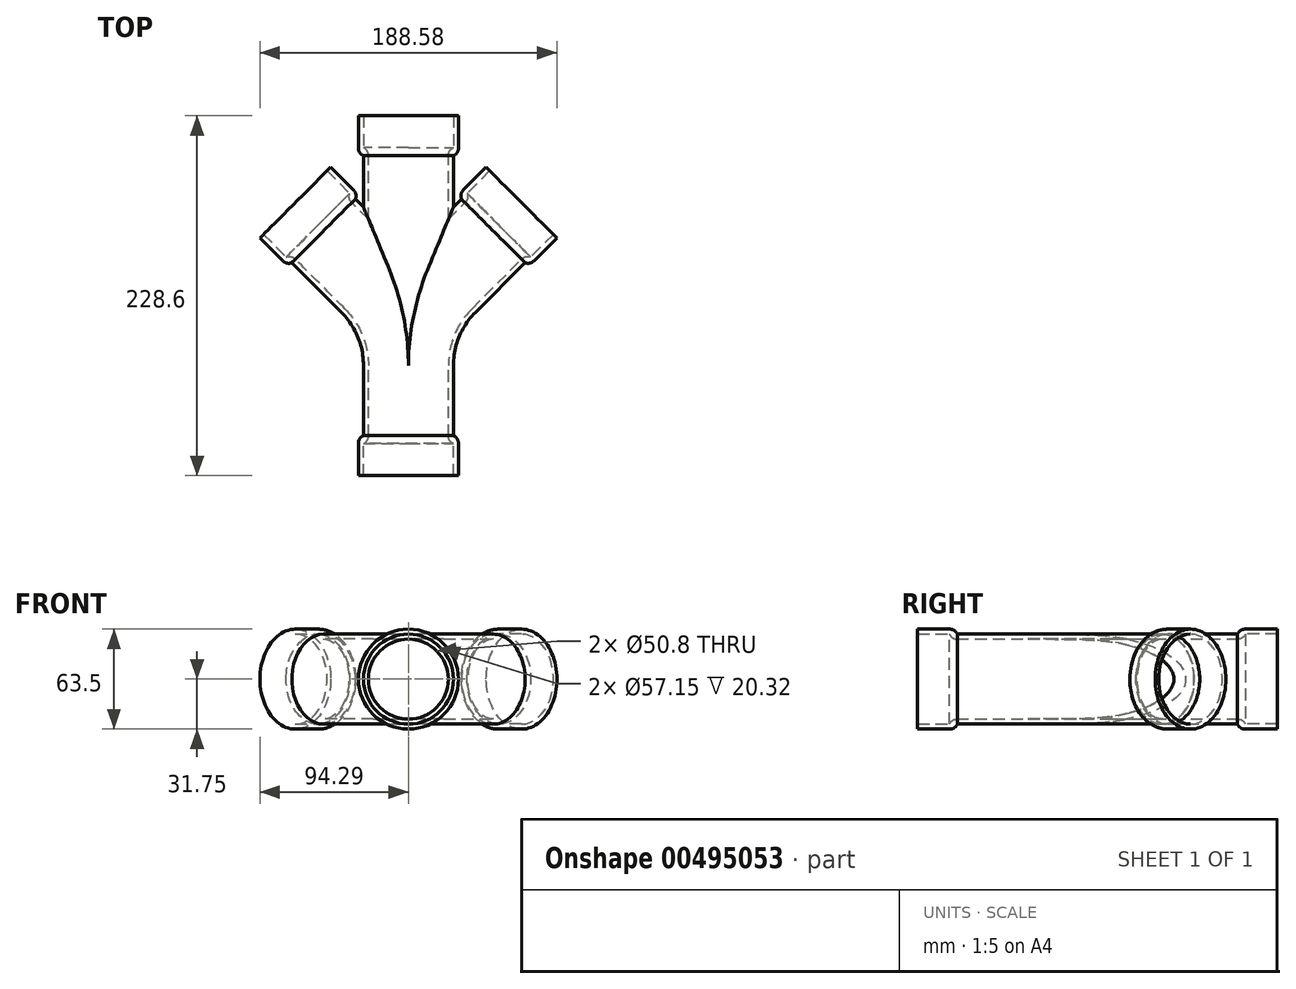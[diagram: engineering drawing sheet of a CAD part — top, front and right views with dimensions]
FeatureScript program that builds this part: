
annotation { "Feature Type Name" : "Feature", "Feature Type Description" : "" }
export const myFeature = defineFeature(function(context is Context, id is Id, definition is map)
    precondition{}
    {
        {
            var Q0;
            Q0=qCreatedBy(makeId("Front.planeOp"),FACE);
            var sketch = newSketch(context, id + "F0", { "sketchPlane" : qUnion([Q0])});
            skCircle(sketch, "E0", {"center": v(0, 0) * mm, "radius": 25.4 * mm});
            skCircle(sketch, "E1", {"center": v(0, 0) * mm, "radius": 28.58 * mm});
            skCircle(sketch, "E2", {"center": v(0, 0) * mm, "radius": 31.75 * mm});
            skCircle(sketch, "E3", {"center": v(0, 0) * mm, "radius": 12.7 * mm});
            skSolve(sketch);
        }
        {
            var Q0;
            Q0=qCreatedBy(makeId("Top.planeOp"),FACE);
            var sketch = newSketch(context, id + "F1", { "sketchPlane" : qUnion([Q0])});
            skLineSegment(sketch, "E4", {"start": v(0, 0) * mm, "end": v(0, 177.8) * mm});
            skLineSegment(sketch, "E5", {"start": v(0, 0) * mm, "end": v(0, 44.64) * mm});
            skLineSegment(sketch, "E6.bottom", {"start": v(0, 76.2) * mm, "end": v(53.88, 76.2) * mm});
            skLineSegment(sketch, "E6.top", {"start": v(0, 130.08) * mm, "end": v(53.88, 130.08) * mm});
            skLineSegment(sketch, "E6.left", {"start": v(0, 76.2) * mm, "end": v(0, 130.08) * mm});
            skLineSegment(sketch, "E6.right", {"start": v(53.88, 76.2) * mm, "end": v(53.88, 130.08) * mm});
            skLineSegment(sketch, "E7.bottom", {"start": v(0, 76.2) * mm, "end": v(-53.88, 76.2) * mm});
            skLineSegment(sketch, "E7.top", {"start": v(0, 130.08) * mm, "end": v(-53.88, 130.08) * mm});
            skLineSegment(sketch, "E7.right", {"start": v(-53.88, 76.2) * mm, "end": v(-53.88, 130.08) * mm});
            skLineSegment(sketch, "E8", {"start": v(22.32, 98.52) * mm, "end": v(53.88, 130.08) * mm});
            skLineSegment(sketch, "E9", {"start": v(-22.32, 98.52) * mm, "end": v(-53.88, 130.08) * mm});
            skPoint(sketch, "E10.visualSharp", {"position": v(0, 76.2) * mm});
            skArc(sketch, "E10.filletArc", {"start": v(22.32, 98.52) * mm, "mid": v(5.8, 73.8) * mm, "end": v(0, 44.64) * mm});
            skArc(sketch, "E11.filletArc", {"start": v(0, 44.64) * mm, "mid": v(-5.8, 73.8) * mm, "end": v(-22.32, 98.52) * mm});
            skSolve(sketch);
        }
        {
            var Q0;
            Q0=makeQuery(id+"F0.imprint","IMPRINT",FACE,{"disambiguationData":[TD([[makeQuery(id+"F0.imprint","IMPRINT",EDGE,{"derivedFrom":sQuery(id+"F0.wireOp",EDGE,"E0")}),-1.0]])]});
            var Q1;
            Q1=sQuery(id+"F1.wireOp",EDGE,"E5");
            var Q2;
            Q2=sQuery(id+"F1.wireOp",EDGE,"E10.filletArc");
            var Q3;
            Q3=sQuery(id+"F1.wireOp",EDGE,"E8");
            sweep(context, id + "F2", {"profiles" : qUnion([Q0]), "path" : qUnion([Q1, Q2, Q3])});
        }
        {
            var Q0;
            Q0=makeQuery(id+"F0.imprint","IMPRINT",FACE,{"disambiguationData":[TD([[makeQuery(id+"F0.imprint","IMPRINT",EDGE,{"derivedFrom":sQuery(id+"F0.wireOp",EDGE,"E0")}),-1.0]])]});
            var Q1;
            Q1=sQuery(id+"F1.wireOp",EDGE,"E5");
            var Q2;
            Q2=sQuery(id+"F1.wireOp",EDGE,"E11.filletArc");
            var Q3;
            Q3=sQuery(id+"F1.wireOp",EDGE,"E9");
            sweep(context, id + "F3", {"operationType" : NewBodyOperationType.ADD, "profiles" : qUnion([Q0]), "path" : qUnion([Q1, Q2, Q3])});
        }
        {
            var Q0;
            Q0=makeQuery(id+"F0.imprint","IMPRINT",FACE,{"disambiguationData":[TD([[makeQuery(id+"F0.imprint","IMPRINT",EDGE,{"derivedFrom":sQuery(id+"F0.wireOp",EDGE,"E0")}),-1.0]])]});
            var Q1;
            Q1=sQuery(id+"F1.wireOp",EDGE,"E4");
            sweep(context, id + "F4", {"operationType" : NewBodyOperationType.ADD, "profiles" : qUnion([Q0]), "path" : qUnion([Q1])});
        }
        {
            var Q0;
            Q0=makeQuery(id+"F0.imprint","IMPRINT",FACE,{"disambiguationData":[TD([[makeQuery(id+"F0.imprint","IMPRINT",EDGE,{"derivedFrom":sQuery(id+"F0.wireOp",EDGE,"E0")}),1.0]])]});
            var Q1;
            Q1=makeQuery(id+"F0.imprint","IMPRINT",FACE,{"disambiguationData":[TD([[makeQuery(id+"F0.imprint","IMPRINT",EDGE,{"derivedFrom":sQuery(id+"F0.wireOp",EDGE,"E3")}),1.0]])]});
            var Q2;
            Q2=sQuery(id+"F1.wireOp",EDGE,"E10.filletArc");
            var Q3;
            Q3=sQuery(id+"F1.wireOp",EDGE,"E8");
            var Q4;
            Q4=sQuery(id+"F1.wireOp",EDGE,"E5");
            sweep(context, id + "F5", {"operationType" : NewBodyOperationType.REMOVE, "profiles" : qUnion([Q0, Q1]), "path" : qUnion([Q2, Q3, Q4])});
        }
        {
            var Q0;
            Q0=makeQuery(id+"F0.imprint","IMPRINT",FACE,{"disambiguationData":[TD([[makeQuery(id+"F0.imprint","IMPRINT",EDGE,{"derivedFrom":sQuery(id+"F0.wireOp",EDGE,"E0")}),1.0]])]});
            var Q1;
            Q1=makeQuery(id+"F0.imprint","IMPRINT",FACE,{"disambiguationData":[TD([[makeQuery(id+"F0.imprint","IMPRINT",EDGE,{"derivedFrom":sQuery(id+"F0.wireOp",EDGE,"E3")}),1.0]])]});
            var Q2;
            Q2=sQuery(id+"F1.wireOp",EDGE,"E5");
            var Q3;
            Q3=sQuery(id+"F1.wireOp",EDGE,"E11.filletArc");
            var Q4;
            Q4=sQuery(id+"F1.wireOp",EDGE,"E9");
            sweep(context, id + "F6", {"operationType" : NewBodyOperationType.REMOVE, "profiles" : qUnion([Q0, Q1]), "path" : qUnion([Q2, Q3, Q4])});
        }
        {
            var Q0;
            Q0=makeQuery(id+"F0.imprint","IMPRINT",FACE,{"disambiguationData":[TD([[makeQuery(id+"F0.imprint","IMPRINT",EDGE,{"derivedFrom":sQuery(id+"F0.wireOp",EDGE,"E0")}),1.0]])]});
            var Q1;
            Q1=makeQuery(id+"F0.imprint","IMPRINT",FACE,{"disambiguationData":[TD([[makeQuery(id+"F0.imprint","IMPRINT",EDGE,{"derivedFrom":sQuery(id+"F0.wireOp",EDGE,"E3")}),1.0]])]});
            var Q2;
            Q2=sQuery(id+"F1.wireOp",EDGE,"E4");
            sweep(context, id + "F7", {"operationType" : NewBodyOperationType.REMOVE, "profiles" : qUnion([Q0, Q1]), "path" : qUnion([Q2])});
        }
        {
            var Q0;
            Q0=makeQuery(id+"F0.imprint","IMPRINT",FACE,{"disambiguationData":[TD([[makeQuery(id+"F0.imprint","IMPRINT",EDGE,{"derivedFrom":sQuery(id+"F0.wireOp",EDGE,"E0")}),-1.0]])]});
            extrude(context, id + "F8", {"entities" : qUnion([Q0]), "operationType" : NewBodyOperationType.ADD, "depth" : 5.08 * mm, "offsetDistance" : 25.4 * mm});
        }
        {
            var Q0;
            Q0=makeQuery(id+"F0.imprint","IMPRINT",FACE,{"disambiguationData":[TD([[makeQuery(id+"F0.imprint","IMPRINT",EDGE,{"derivedFrom":sQuery(id+"F0.wireOp",EDGE,"E1")}),-1.0]])]});
            extrude(context, id + "F9", {"entities" : qUnion([Q0]), "operationType" : NewBodyOperationType.ADD, "depth" : 25.4 * mm, "offsetDistance" : 25.4 * mm});
        }
        {
            var Q0;
            Q0=makeQuery(id+"F2.opSweep","CAP_FACE",FACE,{"disambiguationData":[OSD([sQuery(id+"F0.wireOp",EDGE,"E0"),sQuery(id+"F0.wireOp",EDGE,"E1"),sQuery(id+"F1.wireOp",VERTEX,"E8.end")])],"isStart":false});
            var sketch = newSketch(context, id + "F10", { "sketchPlane" : qUnion([Q0])});
            skCircle(sketch, "E12.0", {"center": v(53.88, 0) * mm, "radius": 28.58 * mm});
            skCircle(sketch, "E13.0", {"center": v(53.88, 0) * mm, "radius": 25.4 * mm});
            skCircle(sketch, "E14", {"center": v(53.88, 0) * mm, "radius": 31.75 * mm});
            skSolve(sketch);
        }
        {
            var Q0;
            Q0=makeQuery(id+"F10.imprint","IMPRINT",FACE,{"disambiguationData":[TD([[makeQuery(id+"F10.imprint","IMPRINT",EDGE,{"derivedFrom":sQuery(id+"F10.wireOp",EDGE,"E12.0")}),1.0]])]});
            extrude(context, id + "F11", {"entities" : qUnion([Q0]), "operationType" : NewBodyOperationType.ADD, "depth" : 5.08 * mm, "offsetDistance" : 25.4 * mm});
        }
        {
            var Q0;
            Q0=makeQuery(id+"F10.imprint","IMPRINT",FACE,{"disambiguationData":[TD([[makeQuery(id+"F10.imprint","IMPRINT",EDGE,{"derivedFrom":sQuery(id+"F10.wireOp",EDGE,"E12.0")}),-1.0]])]});
            extrude(context, id + "F12", {"entities" : qUnion([Q0]), "operationType" : NewBodyOperationType.ADD, "depth" : 25.4 * mm, "offsetDistance" : 25.4 * mm});
        }
        {
            var Q0;
            Q0=makeQuery(id+"F4.opSweep","CAP_FACE",FACE,{"disambiguationData":[OSD([sQuery(id+"F0.wireOp",EDGE,"E0"),sQuery(id+"F0.wireOp",EDGE,"E1"),sQuery(id+"F1.wireOp",VERTEX,"E4.end")])],"isStart":false});
            var sketch = newSketch(context, id + "F13", { "sketchPlane" : qUnion([Q0])});
            skCircle(sketch, "E15.0", {"center": v(0, 0) * mm, "radius": 25.4 * mm});
            skCircle(sketch, "E16.0", {"center": v(0, 0) * mm, "radius": 28.58 * mm});
            skCircle(sketch, "E17", {"center": v(0, 0) * mm, "radius": 31.75 * mm});
            skSolve(sketch);
        }
        {
            var Q0;
            Q0=makeQuery(id+"F13.imprint","IMPRINT",FACE,{"disambiguationData":[TD([[makeQuery(id+"F13.imprint","IMPRINT",EDGE,{"derivedFrom":sQuery(id+"F13.wireOp",EDGE,"E15.0")}),1.0]])]});
            extrude(context, id + "F14", {"entities" : qUnion([Q0]), "operationType" : NewBodyOperationType.ADD, "depth" : 5.08 * mm, "offsetDistance" : 25.4 * mm});
        }
        {
            var Q0;
            Q0=makeQuery(id+"F13.imprint","IMPRINT",FACE,{"disambiguationData":[TD([[makeQuery(id+"F13.imprint","IMPRINT",EDGE,{"derivedFrom":sQuery(id+"F13.wireOp",EDGE,"E16.0")}),-1.0]])]});
            extrude(context, id + "F15", {"entities" : qUnion([Q0]), "operationType" : NewBodyOperationType.ADD, "depth" : 25.4 * mm, "offsetDistance" : 25.4 * mm});
        }
        {
            var Q0;
            Q0=makeQuery(id+"F3.opSweep","CAP_FACE",FACE,{"disambiguationData":[OSD([sQuery(id+"F0.wireOp",EDGE,"E0"),sQuery(id+"F0.wireOp",EDGE,"E1"),sQuery(id+"F1.wireOp",VERTEX,"E9.end")])],"isStart":false});
            var sketch = newSketch(context, id + "F16", { "sketchPlane" : qUnion([Q0])});
            skCircle(sketch, "E18", {"center": v(-53.88, 0) * mm, "radius": 31.75 * mm});
            skSolve(sketch);
        }
        {
            var Q0;
            {var subQ0=sQuery(id+"F1.wireOp",VERTEX,"E9.end");Q0=makeQuery(id+"F16.imprint","IMPRINT",FACE,{"disambiguationData":[TD([[makeQuery(id+"F16.imprint","IMPRINT",EDGE,{"derivedFrom":makeQuery(id+"F3.opSweep","CAP_EDGE",EDGE,{"disambiguationData":[OSD([sQuery(id+"F0.wireOp",EDGE,"E0"),subQ0])],"isStart":false})}),1.0]])]});}
            extrude(context, id + "F17", {"entities" : qUnion([Q0]), "operationType" : NewBodyOperationType.ADD, "depth" : 5.08 * mm, "offsetDistance" : 25.4 * mm});
        }
        {
            var Q0;
            Q0=makeQuery(id+"F16.imprint","IMPRINT",FACE,{"disambiguationData":[TD([[makeQuery(id+"F16.imprint","IMPRINT",EDGE,{"derivedFrom":sQuery(id+"F16.wireOp",EDGE,"E18")}),1.0]])]});
            extrude(context, id + "F18", {"entities" : qUnion([Q0]), "operationType" : NewBodyOperationType.ADD, "depth" : 25.4 * mm, "offsetDistance" : 25.4 * mm});
        }
        {
            var Q0;
            Q0=makeQuery(id+"F15.opExtrude","CAP_EDGE",EDGE,{"disambiguationData":[OSD([sQuery(id+"F13.wireOp",EDGE,"E17")])],"isStart":true});
            var Q1;
            Q1=makeQuery(id+"F18.opExtrude","CAP_EDGE",EDGE,{"disambiguationData":[OSD([sQuery(id+"F16.wireOp",EDGE,"E18")])],"isStart":true});
            var Q2;
            Q2=makeQuery(id+"F12.opExtrude","CAP_EDGE",EDGE,{"disambiguationData":[OSD([sQuery(id+"F10.wireOp",EDGE,"E14")])],"isStart":true});
            var Q3;
            Q3=makeQuery(id+"F9.opExtrude","CAP_EDGE",EDGE,{"disambiguationData":[OSD([sQuery(id+"F0.wireOp",EDGE,"E2")])],"isStart":true});
            var Q4;
            Q4=makeQuery(id+"F14.opExtrude","CAP_EDGE",EDGE,{"disambiguationData":[OSD([sQuery(id+"F13.wireOp",EDGE,"E15.0")])],"isStart":false});
            var Q5;
            Q5=makeQuery(id+"F11.opExtrude","CAP_EDGE",EDGE,{"disambiguationData":[OSD([sQuery(id+"F10.wireOp",EDGE,"E13.0")])],"isStart":false});
            var Q6;
            Q6=makeQuery(id+"F17.opExtrude","CAP_EDGE",EDGE,{"disambiguationData":[OSD([sQuery(id+"F0.wireOp",EDGE,"E0"),sQuery(id+"F1.wireOp",VERTEX,"E9.end")])],"isStart":false});
            var Q7;
            Q7=makeQuery(id+"F8.opExtrude","CAP_EDGE",EDGE,{"disambiguationData":[OSD([sQuery(id+"F0.wireOp",EDGE,"E0")])],"isStart":false});
            fillet(context, id + "F19", {"entities" : qUnion([Q0, Q1, Q2, Q3, Q4, Q5, Q6, Q7]), "radius" : 5.08 * mm, "tangentPropagation" : true, "allowEdgeOverflow" : false});
        }
    });
